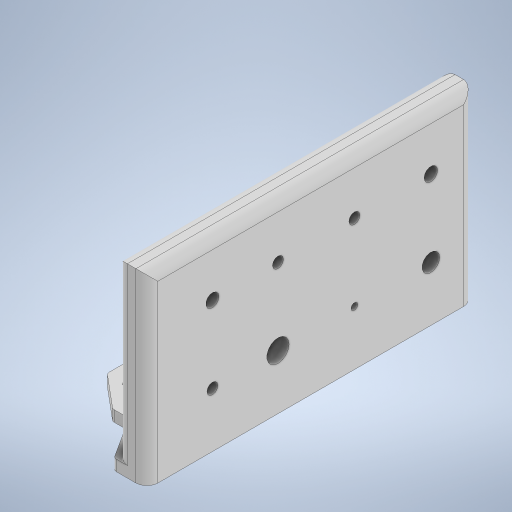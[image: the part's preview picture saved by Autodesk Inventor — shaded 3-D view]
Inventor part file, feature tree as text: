
AUTODESK INVENTOR PART (.ipt)
format: ipt  version: 2024 (Build 280153000, 153)  size: 376,320 bytes
history: native  units: in
note: dims shown in document units (in); Inventor stores cm internally (conversion verified against a paired STEP export)
features: extrude x6, sketch x3, fillet x1
ambient origin geometry x8: Origin, YZ Plane, XZ Plane, XY Plane, X Axis, Y Axis, Z Axis, Center Point
bodies: Body1 (feature_tree)
feature tree (10):
  sketch  "Sketch2"  dims[d18=0.315in d19=0.2008in]
  extrude  "Extrusion11"  Depth=0.2008in
  extrude  "Extrusion12"  Depth=1.5748in
  extrude  "Extrusion13"  Depth=0.1476in
  fillet  "Fillet1"  Radius=0.962in
  sketch  "Sketch6"  dims[d63=1.5748in d64=0.7874in d65=0.962in d66=2.9528in d67=0.5906in d68=0.0787in d69=0.5906in d70=0.0787in d71=0.1969in d72=0.0in d73=0.1181in d74=0.0in d75=3.1496in d76=0.0in d77=0.1969in d79=2.9528in d82=0.9843in d83=1.1811in d84=1.378in d85=1.378in d86=0.7874in d87=0.2362in d88=0.4488in d89=0.1969in d90=0.3937in d91=0.1969in d92=0.2421in d93=0.7874in d94=0.1969in d95=0.4016in d96=0.122in d97=0.3189in d98=0.0in d99=0.0in d100=0.2362in d101=0.0in d102=0.1476in d103=0.0in d45=0.0197in d46=0.0344in d47=0.0197in d48=0.0344in d49=0.0in d50=0.0in]
  extrude  "Extrusion14"  Depth=0.1476in
  extrude  "Extrusion15"  Depth=0.1476in
  extrude  "Extrusion16"  Depth=0.0787in
  sketch  "Sketch5"  dims[d60=5.9055in d62=1.5748in]
